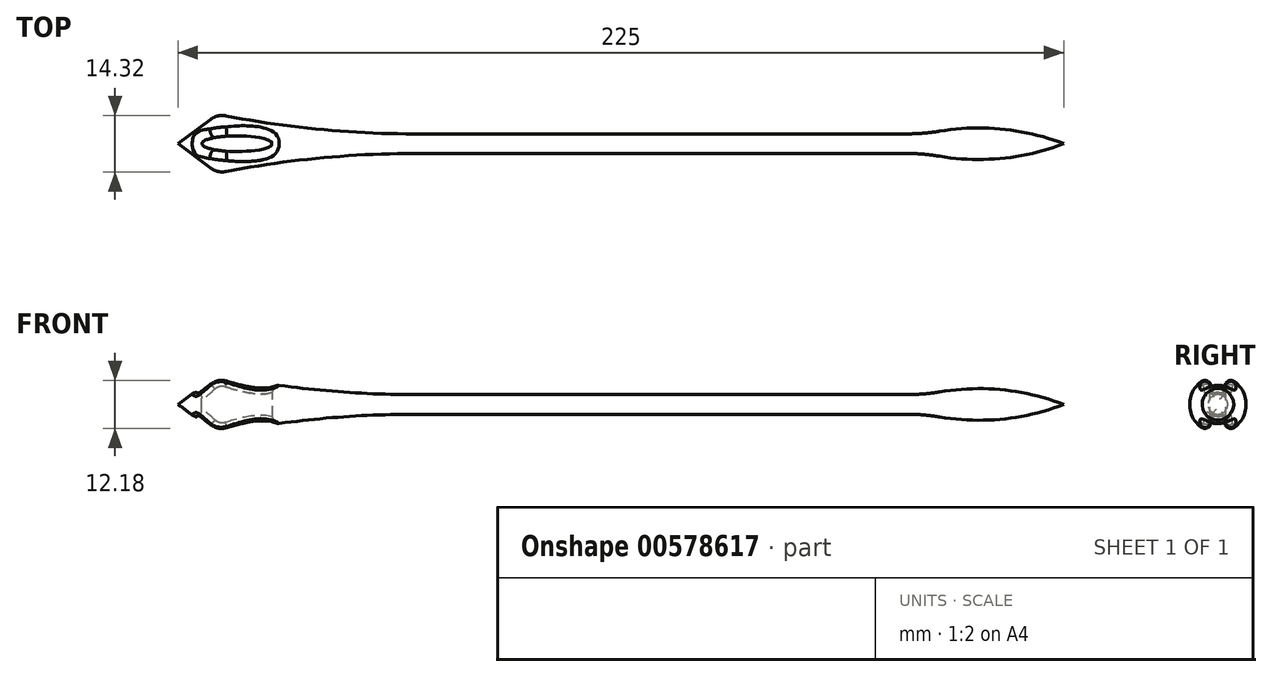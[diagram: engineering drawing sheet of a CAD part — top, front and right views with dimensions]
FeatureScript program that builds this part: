
annotation { "Feature Type Name" : "Feature", "Feature Type Description" : "" }
export const myFeature = defineFeature(function(context is Context, id is Id, definition is map)
    precondition{}
    {
        {
            var Q0;
            Q0=qCreatedBy(makeId("Top.planeOp"),FACE);
            var sketch = newSketch(context, id + "F0", { "sketchPlane" : qUnion([Q0])});
            skLineSegment(sketch, "E0.bottom", {"start": v(0, 0) * mm, "end": v(130, 0) * mm});
            skLineSegment(sketch, "E0.top", {"start": v(0, 2.5) * mm, "end": v(130, 2.5) * mm});
            skLineSegment(sketch, "E0.left", {"start": v(0, 0) * mm, "end": v(0, 2.5) * mm});
            skLineSegment(sketch, "E0.right", {"start": v(130, 0) * mm, "end": v(130, 2.5) * mm});
            skSolve(sketch);
        }
        {
            var Q0;
            Q0=makeQuery(id+"F0.imprint","IMPRINT",FACE,{"disambiguationData":[TD([[makeQuery(id+"F0.imprint","IMPRINT",EDGE,{"derivedFrom":sQuery(id+"F0.wireOp",EDGE,"E0.bottom")}),1.0]])]});
            var Q1;
            Q1=sQuery(id+"F0.wireOp",EDGE,"E0.bottom");
            revolve(context, id + "F1", {"entities" : qUnion([Q0]), "axis" : qUnion([Q1]), "revolveType" : RevolveType.FULL});
        }
        {
            var Q0;
            Q0=qCreatedBy(makeId("Top.planeOp"),FACE);
            var sketch = newSketch(context, id + "F2", { "sketchPlane" : qUnion([Q0])});
            skLineSegment(sketch, "E1", {"start": v(-50, 7.5) * mm, "end": v(0, 2.5) * mm});
            skLineSegment(sketch, "E2", {"start": v(0, 2.5) * mm, "end": v(0, 0) * mm});
            skLineSegment(sketch, "E3", {"start": v(0, 0) * mm, "end": v(-60, 0) * mm});
            skLineSegment(sketch, "E4", {"start": v(-60, 0) * mm, "end": v(-50, 7.5) * mm});
            skSolve(sketch);
        }
        {
            var Q0;
            Q0=makeQuery(id+"F2.imprint","IMPRINT",FACE,{"disambiguationData":[TD([[makeQuery(id+"F2.imprint","IMPRINT",EDGE,{"derivedFrom":sQuery(id+"F2.wireOp",EDGE,"E1")}),-1.0]])]});
            var Q1;
            Q1=sQuery(id+"F2.wireOp",EDGE,"E3");
            revolve(context, id + "F3", {"operationType" : NewBodyOperationType.ADD, "entities" : qUnion([Q0]), "axis" : qUnion([Q1]), "revolveType" : RevolveType.FULL});
        }
        {
            var Q0;
            Q0=qCreatedBy(makeId("Top.planeOp"),FACE);
            var sketch = newSketch(context, id + "F4", { "sketchPlane" : qUnion([Q0])});
            skArc(sketch, "E5", {"start": v(-50, 7.5) * mm, "mid": v(-25.12, 3.75) * mm, "end": v(0, 2.5) * mm});
            skLineSegment(sketch, "E6", {"start": v(0, 2.5) * mm, "end": v(9.33, 2.5) * mm, "construction": true});
            skLineSegment(sketch, "E7", {"start": v(-50, 7.5) * mm, "end": v(0, 2.5) * mm});
            skSolve(sketch);
        }
        {
            var Q0;
            Q0 = qSketchRegion(id + "F4", true);
            var Q1;
            Q1=makeQuery(id+"F3.opRevolve","SWEPT_FACE",FACE,{"disambiguationData":[OSD([sQuery(id+"F2.wireOp",EDGE,"E1")])]});
            revolve(context, id + "F5", {"operationType" : NewBodyOperationType.REMOVE, "entities" : qUnion([Q0]), "axis" : qUnion([Q1]), "revolveType" : RevolveType.FULL, "oppositeDirection" : true});
        }
        {
            var Q0;
            Q0=qCreatedBy(makeId("Top.planeOp"),FACE);
            var sketch = newSketch(context, id + "F6", { "sketchPlane" : qUnion([Q0])});
            skEllipse(sketch, "E8", {"center": v(-45, 0) * mm, "majorRadius": 9 * mm, "minorRadius": 2 * mm, "majorAxis": v(1, 0)});
            skSolve(sketch);
        }
        {
            var Q0;
            Q0 = qSketchRegion(id + "F6", true);
            extrude(context, id + "F7", {"entities" : qUnion([Q0]), "operationType" : NewBodyOperationType.REMOVE, "oppositeDirection" : true, "depth" : 25 * mm, "offsetDistance" : 25 * mm, "hasSecondDirection" : true, "secondDirectionOppositeDirection" : false, "secondDirectionDepth" : 25 * mm});
        }
        {
            var Q0;
            {var subQ0=sQuery(id+"F4.wireOp",EDGE,"E7");var subQ1=sQuery(id+"F4.wireOp",EDGE,"E5");Q0=makeQuery(id+"F7.boolean.opBoolean","SPLIT",EDGE,{"disambiguationData":[OD(0.0)],"derivedFrom":makeQuery(id+"F5.boolean.opBoolean","MERGE",EDGE,{"derivedFrom":[makeQuery(id+"F3.opRevolve","SWEPT_EDGE",EDGE,{"disambiguationData":[OSD([sQuery(id+"F2.wireOp",EDGE,"E1"),sQuery(id+"F2.wireOp",EDGE,"E4")])]}),makeQuery(id+"F5.opRevolve","SWEPT_EDGE",EDGE,{"disambiguationData":[OSD([subQ1,subQ0]),TDD([makeQuery(id+"F4.imprint","INTERSECT",VERTEX,{"disambiguationData":[OD(0.0)],"derivedFrom":[subQ1,subQ0]})])]})]})});}
            var Q1;
            {var subQ0=sQuery(id+"F4.wireOp",EDGE,"E7");var subQ1=sQuery(id+"F4.wireOp",EDGE,"E5");Q1=makeQuery(id+"F7.boolean.opBoolean","SPLIT",EDGE,{"disambiguationData":[OD(1.0)],"derivedFrom":makeQuery(id+"F5.boolean.opBoolean","MERGE",EDGE,{"derivedFrom":[makeQuery(id+"F3.opRevolve","SWEPT_EDGE",EDGE,{"disambiguationData":[OSD([sQuery(id+"F2.wireOp",EDGE,"E1"),sQuery(id+"F2.wireOp",EDGE,"E4")])]}),makeQuery(id+"F5.opRevolve","SWEPT_EDGE",EDGE,{"disambiguationData":[OSD([subQ1,subQ0]),TDD([makeQuery(id+"F4.imprint","INTERSECT",VERTEX,{"disambiguationData":[OD(0.0)],"derivedFrom":[subQ1,subQ0]})])]})]})});}
            fillet(context, id + "F8", {"entities" : qUnion([Q0, Q1]), "radius" : 5 * mm, "tangentPropagation" : true, "allowEdgeOverflow" : false});
        }
        {
            var Q0;
            Q0=makeQuery(id+"F7.boolean.opBoolean","COPY",FACE,{"derivedFrom":makeQuery(id+"F7.opExtrude","SWEPT_FACE",FACE,{"disambiguationData":[OSD([sQuery(id+"F6.wireOp",EDGE,"E8")])]})});
            fillet(context, id + "F9", {"entities" : qUnion([Q0]), "radius" : 1.5 * mm, "tangentPropagation" : true, "allowEdgeOverflow" : false});
        }
        {
            var Q0;
            Q0=qCreatedBy(makeId("Top.planeOp"),FACE);
            var sketch = newSketch(context, id + "F10", { "sketchPlane" : qUnion([Q0])});
            skLineSegment(sketch, "E9", {"start": v(130, 0) * mm, "end": v(130, 2.5) * mm});
            skLineSegment(sketch, "E10", {"start": v(140, 5) * mm, "end": v(130, 2.5) * mm, "construction": true});
            skLineSegment(sketch, "E11", {"start": v(140, 5) * mm, "end": v(155, 3) * mm, "construction": true});
            skLineSegment(sketch, "E12", {"start": v(165, 0) * mm, "end": v(155, 3) * mm, "construction": true});
            skLineSegment(sketch, "E13", {"start": v(165, 0) * mm, "end": v(130, 0) * mm});
            skArc(sketch, "E14", {"start": v(165, 0) * mm, "mid": v(147.69, 3.86) * mm, "end": v(130, 2.5) * mm});
            skSolve(sketch);
        }
        {
            var Q0;
            Q0=makeQuery(id+"F10.imprint","IMPRINT",FACE,{"disambiguationData":[TD([[makeQuery(id+"F10.imprint","IMPRINT",EDGE,{"derivedFrom":sQuery(id+"F10.wireOp",EDGE,"E9")}),-1.0]])]});
            var Q1;
            Q1=sQuery(id+"F10.wireOp",EDGE,"E13");
            revolve(context, id + "F11", {"operationType" : NewBodyOperationType.ADD, "entities" : qUnion([Q0]), "axis" : qUnion([Q1]), "revolveType" : RevolveType.FULL});
        }
        {
            var Q0;
            Q0=makeQuery(id+"F11.boolean.opBoolean","MERGE",EDGE,{"derivedFrom":[makeQuery(id+"F1.opRevolve","SWEPT_EDGE",EDGE,{"disambiguationData":[OSD([sQuery(id+"F0.wireOp",EDGE,"E0.top"),sQuery(id+"F0.wireOp",EDGE,"E0.right")])]}),makeQuery(id+"F11.opRevolve","SWEPT_EDGE",EDGE,{"disambiguationData":[OSD([sQuery(id+"F10.wireOp",EDGE,"E9"),sQuery(id+"F10.wireOp",EDGE,"E14")])]})]});
            fillet(context, id + "F12", {"entities" : qUnion([Q0]), "radius" : 50 * mm, "tangentPropagation" : true, "allowEdgeOverflow" : false});
        }
    });
